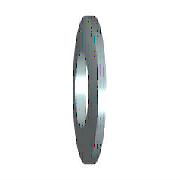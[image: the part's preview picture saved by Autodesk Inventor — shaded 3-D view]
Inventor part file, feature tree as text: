
AUTODESK INVENTOR PART (.ipt)
format: ipt  version: 2018 (Build 220112000, 112)  size: 117,760 bytes
history: native  units: mm (DEFAULTED — no unit token found)
features: other x2, plane x1
ambient origin geometry x7: Origin, YZ Plane, XY Plane, X Axis, Y Axis, Z Axis, Center Point
bodies: Solid1 (feature_tree)
feature tree (3):
  other  "IDS_BODY"
  other  "Work Axis1"
  plane  "Work Plane1"
